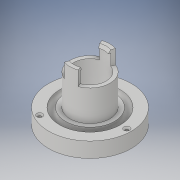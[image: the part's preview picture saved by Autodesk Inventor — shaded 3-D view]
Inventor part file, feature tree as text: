
AUTODESK INVENTOR PART (.ipt)
format: ipt  version: 2019 (Build 230136000, 136)  size: 203,264 bytes
history: native  units: mm
features: sketch x6, extrude x4, revolve x2, chamfer x1
ambient origin geometry x8: Origin, YZ Plane, XZ Plane, XY Plane, X Axis, Y Axis, Z Axis, Center Point
bodies: Solid1 (feature_tree)
feature tree (13):
  extrude  "Extrusion1"  Depth=110.0mm
  revolve  "Revolution1"  [1 undecoded]
  extrude  "Extrusion2"  TaperAngle=90.0deg  [1 undecoded]
  revolve  "Revolution2"  [1 undecoded]
  extrude  "Extrusion3"  Depth=43.0mm
  extrude  "Extrusion4"  Depth=2.0mm
  chamfer  "Chamfer2"  Distance=6.981317mm
  sketch  "Sketch1"  dims[d0=43.0mm d1=110.0mm]
  sketch  "Sketch2"  dims[d2=20.0mm d3=0.0mm d4=10.0mm]
  sketch  "Sketch3"  dims[d5=15.0mm d6=90.0deg]
  sketch  "Sketch4"  dims[d7=60.0mm d8=0.0mm d9=2.5mm]
  sketch  "Sketch5"  dims[d10=90.0deg d18=43.0mm]
  sketch  "Sketch6"  dims[d19=43.0mm d20=53.0mm d22=6.981317mm d23=6.981317mm d24=3.490659mm d25=3.490659mm d26=24.43461mm d27=24.43461mm d28=19.0mm d29=0.0mm d30=30.0mm d32=360.0deg d34=18.0mm d35=0.0mm d39=2.0mm d40=2.0mm d41=45.0deg]
note: 3 required parameter values undecoded (feature->parameter linkage not recoverable at this tier; creation-order binding heuristic only, values carry confidence <= 0.55)